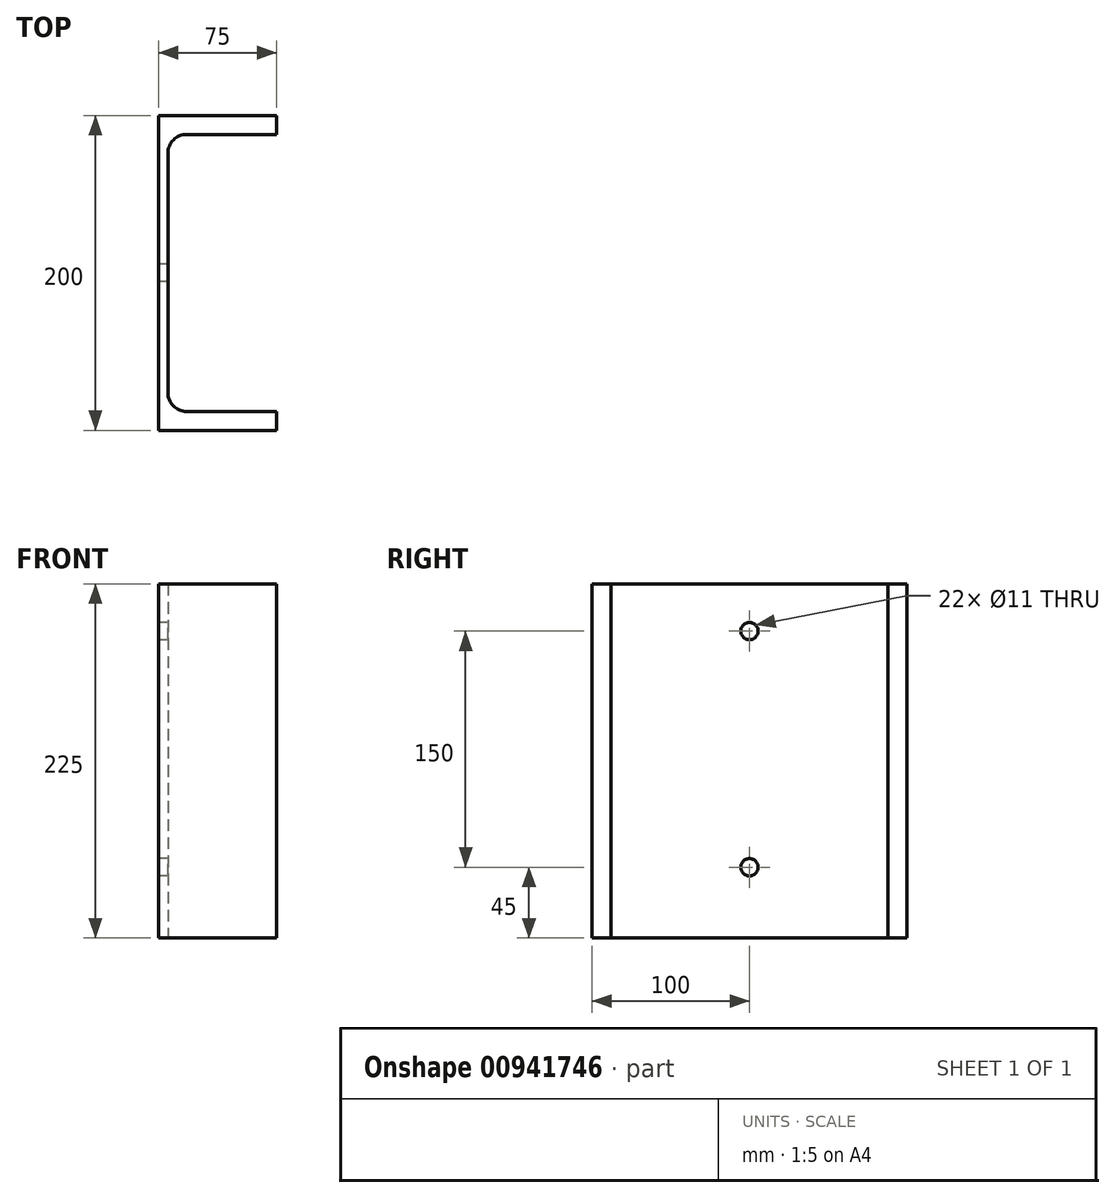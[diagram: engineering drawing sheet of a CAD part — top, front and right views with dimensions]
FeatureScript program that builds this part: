
annotation { "Feature Type Name" : "Feature", "Feature Type Description" : "" }
export const myFeature = defineFeature(function(context is Context, id is Id, definition is map)
    precondition{}
    {
        {
            var Q0;
            Q0=qCreatedBy(makeId("Top.planeOp"),FACE);
            var sketch = newSketch(context, id + "F0", { "sketchPlane" : qUnion([Q0])});
            skLineSegment(sketch, "E0", {"start": v(0, 0) * mm, "end": v(0, 200) * mm});
            skLineSegment(sketch, "E1", {"start": v(0, 200) * mm, "end": v(75, 200) * mm});
            skLineSegment(sketch, "E2", {"start": v(75, 200) * mm, "end": v(75, 188) * mm});
            skLineSegment(sketch, "E3", {"start": v(75, 188) * mm, "end": v(18, 188) * mm});
            skLineSegment(sketch, "E4", {"start": v(6, 176) * mm, "end": v(6, 24) * mm});
            skLineSegment(sketch, "E5", {"start": v(18, 12) * mm, "end": v(75, 12) * mm});
            skLineSegment(sketch, "E6", {"start": v(75, 12) * mm, "end": v(75, 0) * mm});
            skLineSegment(sketch, "E7", {"start": v(75, 0) * mm, "end": v(0, 0) * mm});
            skPoint(sketch, "E8.visualSharp", {"position": v(6, 188) * mm});
            skArc(sketch, "E8.filletArc", {"start": v(18, 188) * mm, "mid": v(9.51, 184.49) * mm, "end": v(6, 176) * mm});
            skPoint(sketch, "E9.visualSharp", {"position": v(6, 12) * mm});
            skArc(sketch, "E9.filletArc", {"start": v(6, 24) * mm, "mid": v(9.51, 15.51) * mm, "end": v(18, 12) * mm});
            skSolve(sketch);
        }
        {
            var Q0;
            Q0=makeQuery(id+"F0.imprint","IMPRINT",FACE,{"disambiguationData":[TD([[makeQuery(id+"F0.imprint","IMPRINT",EDGE,{"derivedFrom":sQuery(id+"F0.wireOp",EDGE,"E0")}),-1.0]])]});
            extrude(context, id + "F1", {"entities" : qUnion([Q0]), "depth" : 225 * mm, "offsetDistance" : 25 * mm});
        }
        {
            var Q0;
            Q0=qCreatedBy(makeId("Right.planeOp"),FACE);
            var sketch = newSketch(context, id + "F2", { "sketchPlane" : qUnion([Q0])});
            skCircle(sketch, "E10", {"center": v(100, 195) * mm, "radius": 5.5 * mm});
            skCircle(sketch, "E11", {"center": v(100, 45) * mm, "radius": 5.5 * mm});
            skLineSegment(sketch, "E12", {"start": v(100, 225) * mm, "end": v(100, 0) * mm, "construction": true});
            skSolve(sketch);
        }
        {
            var Q0;
            Q0 = qSketchRegion(id + "F2", true);
            extrude(context, id + "F3", {"entities" : qUnion([Q0]), "operationType" : NewBodyOperationType.REMOVE, "endBound" : BoundingType.THROUGH_ALL, "depth" : 25 * mm, "offsetDistance" : 25 * mm});
        }
    });
